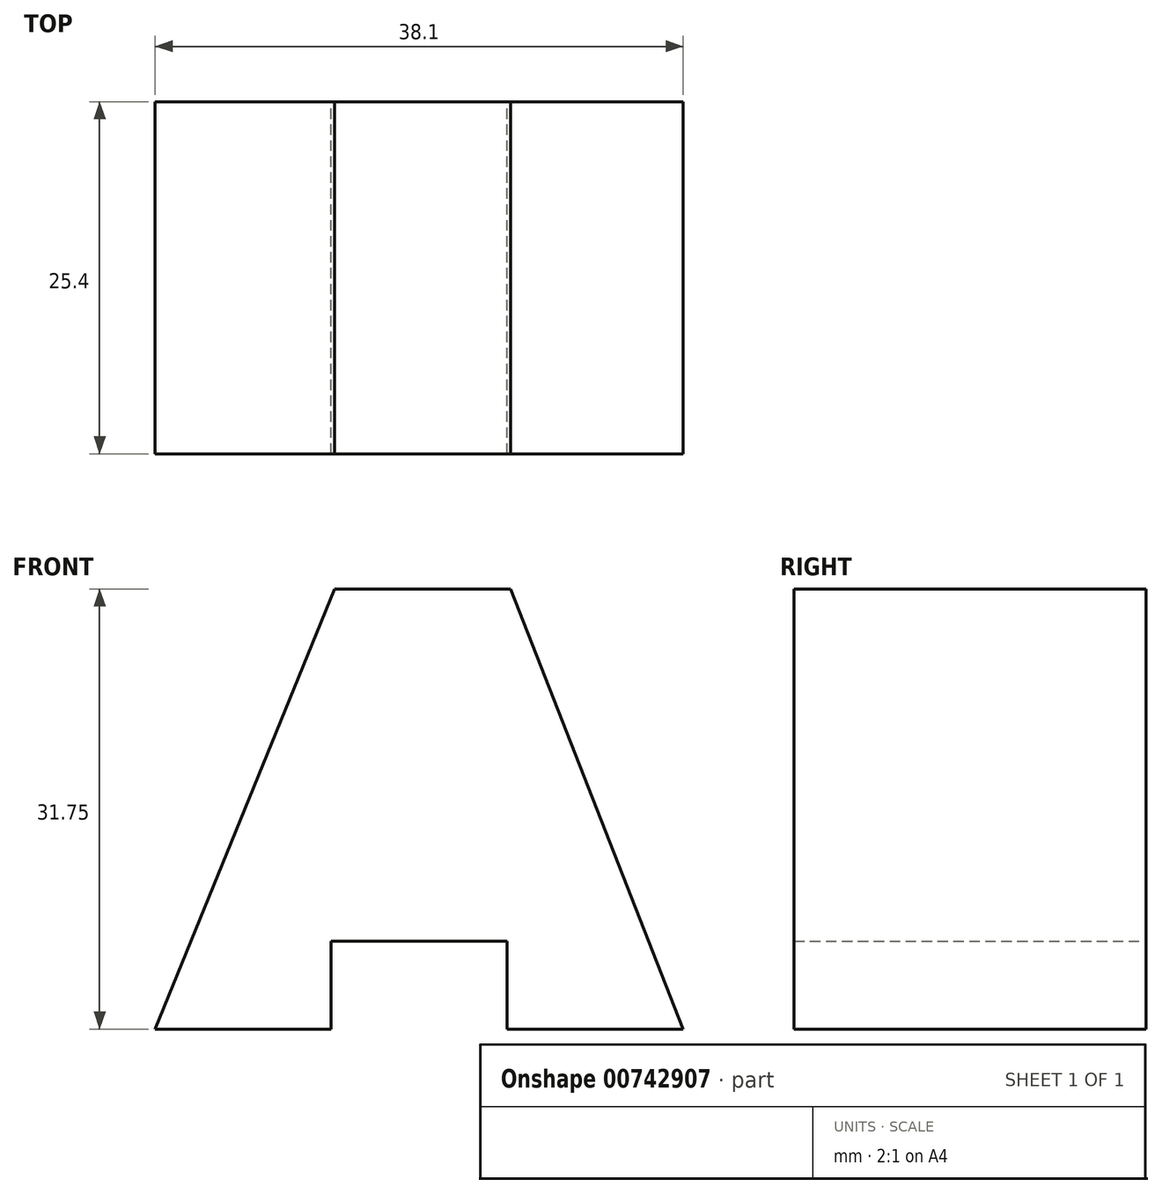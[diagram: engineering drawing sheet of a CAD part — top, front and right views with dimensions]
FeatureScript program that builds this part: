
annotation { "Feature Type Name" : "Feature", "Feature Type Description" : "" }
export const myFeature = defineFeature(function(context is Context, id is Id, definition is map)
    precondition{}
    {
        {
            var Q0;
            Q0=qCreatedBy(makeId("Front.planeOp"),FACE);
            var sketch = newSketch(context, id + "F0", { "sketchPlane" : qUnion([Q0])});
            skLineSegment(sketch, "E0", {"start": v(0, 0) * mm, "end": v(12.7, 0) * mm});
            skLineSegment(sketch, "E1", {"start": v(12.7, 0) * mm, "end": v(12.7, 6.35) * mm});
            skLineSegment(sketch, "E2", {"start": v(12.7, 6.35) * mm, "end": v(25.4, 6.35) * mm});
            skLineSegment(sketch, "E3", {"start": v(25.4, 6.35) * mm, "end": v(25.4, 0) * mm});
            skLineSegment(sketch, "E4", {"start": v(25.4, 0) * mm, "end": v(38.1, 0) * mm});
            skLineSegment(sketch, "E5", {"start": v(38.1, 0) * mm, "end": v(25.65, 31.75) * mm});
            skLineSegment(sketch, "E6", {"start": v(25.65, 31.75) * mm, "end": v(12.95, 31.75) * mm});
            skLineSegment(sketch, "E7", {"start": v(12.95, 31.75) * mm, "end": v(0, 0) * mm});
            skSolve(sketch);
        }
        {
            var Q0;
            Q0=makeQuery(id+"F0.imprint","IMPRINT",FACE,{"disambiguationData":[TD([[makeQuery(id+"F0.imprint","IMPRINT",EDGE,{"derivedFrom":sQuery(id+"F0.wireOp",EDGE,"E0")}),1.0]])]});
            extrude(context, id + "F1", {"entities" : qUnion([Q0]), "depth" : 25.4 * mm, "offsetDistance" : 25.4 * mm});
        }
    });
